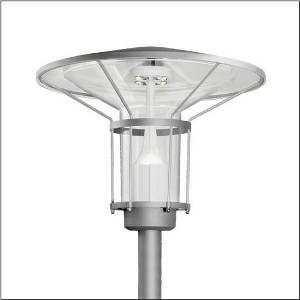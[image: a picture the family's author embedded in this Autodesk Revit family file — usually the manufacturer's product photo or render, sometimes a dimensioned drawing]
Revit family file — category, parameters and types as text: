
# Revit family: laterne_classic_iq___st1_2a_5xa5245ef14h_7fcb
name_source: partatom
category: Lighting Fixtures
units: mm (PartAtom-declared; Revit-internal decimal feet)

## family parameters
Cut with Voids When Loaded = No
Host = Face
Light Source = No
Part Type = Normal
Room Calculation Point = No
Round Connector Dimension = Use Diameter
Shared = No

## types (1)
- --- (1 x LED, 1380 lm, 10.5 W, 3000K)
    Apparent Load = 11 VA
    CIE Flux Codes = 21 60 93 97 100
    Color Rendering = 70
    Color Temperature = 3000K
    Default Elevation = 1800 mm
    Description = Lantern Classic iQ, mast luminaire, Module 540 iQ-SR, primary light control with 3 zone facetted reflector, of plastic, silver coated, highly specular, structured, primary optical cover: cover, of PMMA, transparent, light distribution: ST1.2a, light emission: direct distribution, primary light characteristic: asymmetric, installation type: post-top, LED, High Power LED, rated luminous flux: 1.380lm, luminous efficacy: 131lm/W, light colour: 730, colour temperature: 3000K, control gear: iQ Street-Remote, control: Auto-Match, Temp-Guard, Lumen-Switch, Night-Set, Smart-Wire, Light-Fading, Desk-Remote (wireless, voltage-free reading and setting of iQ features in the workshop via application-optimized NFC function/RFID function), optimised constant luminous flux control (CLO 2.0), Street-Remote, pre-setting: logarithmic dimming characteristic, with terminal, 6-pole, max. 2.5mm², mains connection: 230..240V, AC, 50/60Hz, start of lifetime: 11W, end of service life: 11W, reduction: 5W, luminaire housing, upper part, of glass-fibre reinforced polyester, coated, Siteco® metallic grey (DB 702S), diameter: 750mm, height: 596mm, spigot size: d x l = 76 x 70mm (post-top) | with reducer (optional accessory) 60 x 70mm, mounting height: 3..5m, post-top mast mounting element, of diecast aluminium, coated, Siteco® metallic grey (DB 702S), Module 540 iQ-SR, traffic white (RAL 9016), equipment: standard, protection rating (complete): IP65, insulation class (complete): insulation class II (safety insulation), certification: CE, ENEC, VDE, packaging unit: 1 piece

Light Distribution: ST1.2a
    Height = 596 mm
    Lamp = 1 x LED
    Lamp Light Flux = 1380 lm
    Lamp Power = 10.5 W
    Lamp count = 1
    Length = 750 mm
    Luminous efficacy = 131 lm/W
    Manufacturer = Siteco
    ModVariant = No
    Model = 5XA5245EF14H
    Number of Poles = 1
    OnlyDefault = Yes
    Power Factor = 1
    Product Name = Laterne Classic iQ | ST1.2a
    Product group = mast luminaire | pylon top
    ProductGroupID = 6100
    Protection Class = Protection class II
    Protection Degree = IP 65
    RLX_Detail_Level = 1
    RLX_Emergency_Light_Flux = 0 lm
    RLX_Emergency_Type = 0
    RLX_Emergency_Type_DB = No
    RlxData = <blob elided: 92005 chars, md5=445c00cc>
    Socket = socket
    Standby Power = 0 W
    System Light Flux = 1380 lm
    System Power = 11 W
    Type Comments = factory setting: luminous flux: 100 % | dim-lin: 254 | 419 mA
    Type Image = l_1006052.jpg
    URL = http://relux.com
    VarID = @adj_181841
    Voltage = 0 V
    Weight = 0.00 kg
    Width = 0 mm  [stored 0 ft]

note: [stored X ft] marks values corroborated as IEEE doubles in the binary element streams (Revit-internal decimal feet)

## geometry (parser evidence)
native form markers: Blend x4, Sweep x12
no freeform markers — native parametric forms only
